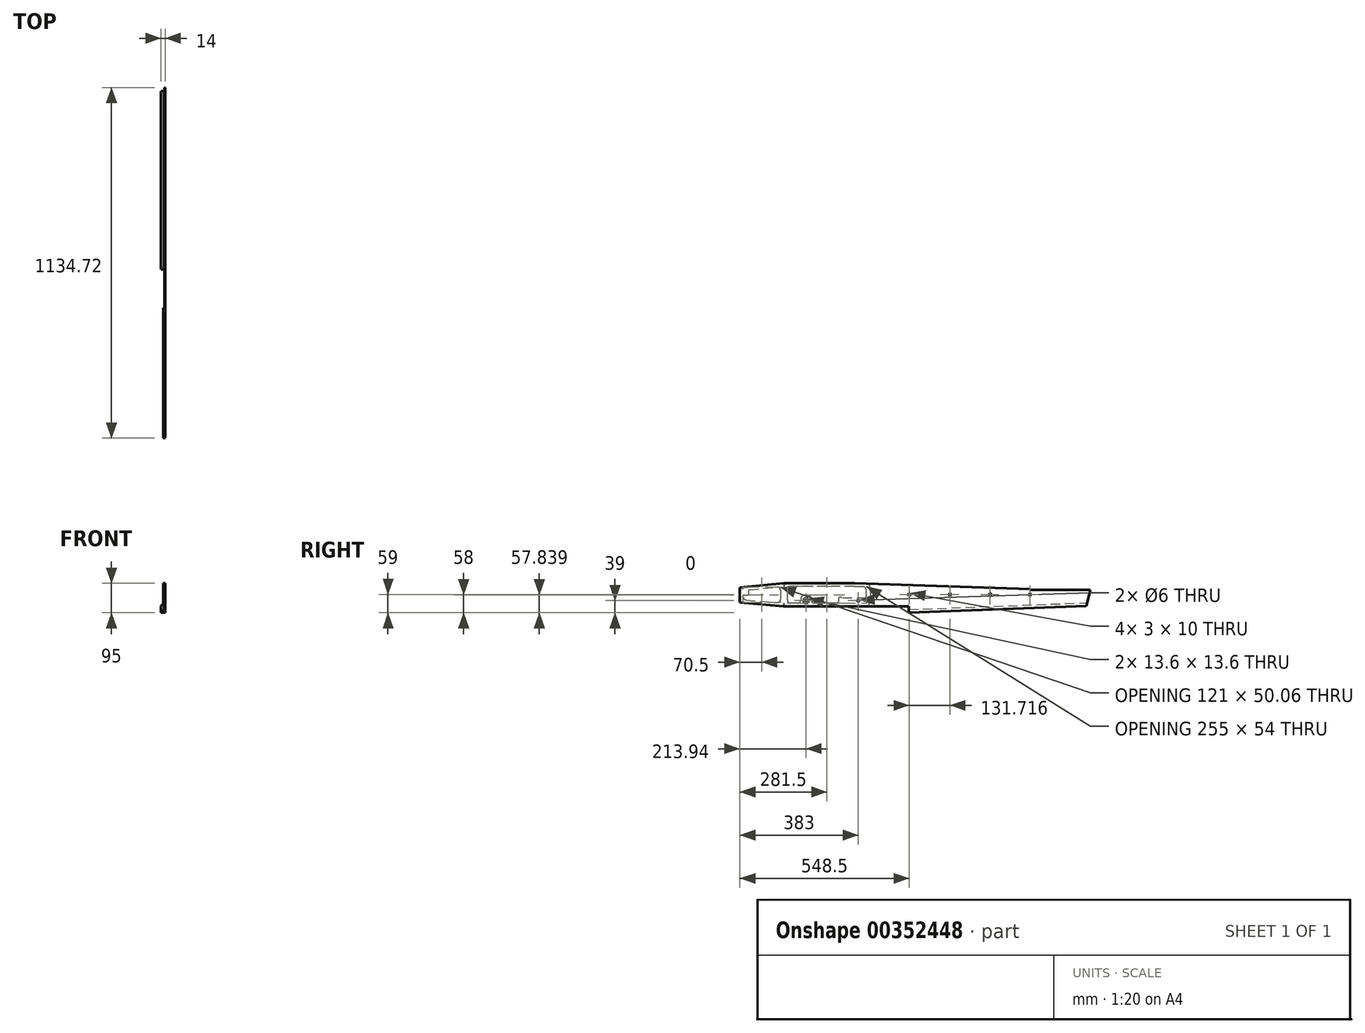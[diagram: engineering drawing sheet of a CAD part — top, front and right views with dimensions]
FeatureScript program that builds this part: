
annotation { "Feature Type Name" : "Feature", "Feature Type Description" : "" }
export const myFeature = defineFeature(function(context is Context, id is Id, definition is map)
    precondition{}
    {
        {
            var Q0;
            Q0=qCreatedBy(makeId("Right.planeOp"),FACE);
            var sketch = newSketch(context, id + "F0", { "sketchPlane" : qUnion([Q0])});
            skLineSegment(sketch, "E0", {"start": v(-571.5, 0) * mm, "end": v(571.5, 0) * mm, "construction": true});
            skLineSegment(sketch, "E1", {"start": v(-571.5, 22) * mm, "end": v(-571.5, -26) * mm});
            skLineSegment(sketch, "E2", {"start": v(-571.5, 22) * mm, "end": v(-430.5, 36) * mm});
            skLineSegment(sketch, "E3", {"start": v(-430.5, 36) * mm, "end": v(-200.5, 36) * mm});
            skLineSegment(sketch, "E4", {"start": v(-200.5, 36) * mm, "end": v(369.22, 18) * mm});
            skLineSegment(sketch, "E5", {"start": v(369.22, 18) * mm, "end": v(369.22, 15) * mm});
            skLineSegment(sketch, "E6", {"start": v(369.22, 15) * mm, "end": v(563.22, 15) * mm});
            skLineSegment(sketch, "E7", {"start": v(-571.5, -26) * mm, "end": v(-430.5, -38) * mm});
            skLineSegment(sketch, "E8", {"start": v(-430.5, -38) * mm, "end": v(-24.5, -38) * mm});
            skLineSegment(sketch, "E9", {"start": v(-24.5, -38) * mm, "end": v(-24.5, -59) * mm});
            skLineSegment(sketch, "E10", {"start": v(-24.5, -59) * mm, "end": v(551.06, -36.59) * mm});
            skLineSegment(sketch, "E11", {"start": v(563.22, 15) * mm, "end": v(551.06, -36.59) * mm});
            skLineSegment(sketch, "E12", {"start": v(-175.5, 35.21) * mm, "end": v(-175.5, -38) * mm, "construction": true});
            skPoint(sketch, "E13", {"position": v(-175.5, -38) * mm});
            skPoint(sketch, "E14", {"position": v(-175.5, 35.21) * mm});
            skLineSegment(sketch, "E15", {"start": v(-458.5, -20) * mm, "end": v(-113.5, -20) * mm, "construction": true});
            skLineSegment(sketch, "E16.bottom", {"start": v(-350.76, -13.2) * mm, "end": v(-364.36, -13.2) * mm});
            skLineSegment(sketch, "E16.top", {"start": v(-350.76, -26.8) * mm, "end": v(-364.36, -26.8) * mm});
            skLineSegment(sketch, "E16.left", {"start": v(-350.76, -13.2) * mm, "end": v(-350.76, -26.8) * mm});
            skLineSegment(sketch, "E16.right", {"start": v(-364.36, -13.2) * mm, "end": v(-364.36, -26.8) * mm});
            skPoint(sketch, "E16.middle", {"position": v(-357.56, -20) * mm});
            skLineSegment(sketch, "E17", {"start": v(369.22, 15) * mm, "end": v(369.22, -43.67) * mm, "construction": true});
            skLineSegment(sketch, "E18", {"start": v(369.22, -5) * mm, "end": v(366.22, -5) * mm});
            skLineSegment(sketch, "E19", {"start": v(366.22, -5) * mm, "end": v(366.22, 5) * mm});
            skLineSegment(sketch, "E20", {"start": v(366.22, 5) * mm, "end": v(369.22, 5) * mm});
            skLineSegment(sketch, "E21.bottom", {"start": v(237.22, 5) * mm, "end": v(240.22, 5) * mm});
            skLineSegment(sketch, "E21.top", {"start": v(237.22, -5) * mm, "end": v(240.22, -5) * mm});
            skLineSegment(sketch, "E21.left", {"start": v(237.22, 5) * mm, "end": v(237.22, -5) * mm});
            skLineSegment(sketch, "E21.right", {"start": v(240.22, 5) * mm, "end": v(240.22, -5) * mm});
            skPoint(sketch, "E21.middle", {"position": v(238.72, 0) * mm});
            skLineSegment(sketch, "E22.bottom", {"start": v(107.22, 5) * mm, "end": v(110.22, 5) * mm});
            skLineSegment(sketch, "E22.top", {"start": v(107.22, -5) * mm, "end": v(110.22, -5) * mm});
            skLineSegment(sketch, "E22.left", {"start": v(107.22, 5) * mm, "end": v(107.22, -5) * mm});
            skLineSegment(sketch, "E22.right", {"start": v(110.22, 5) * mm, "end": v(110.22, -5) * mm});
            skPoint(sketch, "E22.middle", {"position": v(108.72, 0) * mm});
            skLineSegment(sketch, "E23.bottom", {"start": v(-21.5, 5) * mm, "end": v(-24.5, 5) * mm});
            skLineSegment(sketch, "E23.top", {"start": v(-21.5, -5) * mm, "end": v(-24.5, -5) * mm});
            skLineSegment(sketch, "E23.left", {"start": v(-21.5, 5) * mm, "end": v(-21.5, -5) * mm});
            skLineSegment(sketch, "E23.right", {"start": v(-24.5, 5) * mm, "end": v(-24.5, -5) * mm});
            skPoint(sketch, "E23.middle", {"position": v(-23, 0) * mm});
            skLineSegment(sketch, "E24", {"start": v(369.22, 5) * mm, "end": v(369.22, -5) * mm});
            skLineSegment(sketch, "E25", {"start": v(107.22, 26.28) * mm, "end": v(107.22, -53.87) * mm, "construction": true});
            skLineSegment(sketch, "E26", {"start": v(237.22, 22.17) * mm, "end": v(237.22, -48.8) * mm, "construction": true});
            skCircle(sketch, "E27", {"center": v(-188.5, -20) * mm, "radius": 3 * mm});
            skLineSegment(sketch, "E28", {"start": v(-24.5, -38) * mm, "end": v(-24.5, 30.44) * mm, "construction": true});
            skSolve(sketch);
        }
        {
            var Q0;
            Q0=makeQuery(id+"F0.imprint","IMPRINT",FACE,{"disambiguationData":[TD([[makeQuery(id+"F0.imprint","IMPRINT",EDGE,{"derivedFrom":sQuery(id+"F0.wireOp",EDGE,"E1")}),1.0]])]});
            extrude(context, id + "F1", {"entities" : qUnion([Q0]), "offsetDistance" : 25 * mm, "depth" : 3 * mm, "symmetric" : true});
        }
        {
            var Q0;
            Q0=makeQuery(id+"F1.opExtrude","SWEPT_FACE",FACE,{"disambiguationData":[OSD([sQuery(id+"F0.wireOp",EDGE,"E9")])]});
            cPlane(context, id + "F2", {"entities" : qUnion([Q0]), "cplaneType" : CPlaneType.OFFSET, "offset" : 0 * mm, "width" : 150 * mm, "height" : 150 * mm});
        }
        {
            var Q0;
            Q0=qCreatedBy(id+"F2.planeOp",FACE);
            var sketch = newSketch(context, id + "F3", { "sketchPlane" : qUnion([Q0])});
            skLineSegment(sketch, "E29", {"start": v(2.5, -59) * mm, "end": v(12.5, -59) * mm});
            skLineSegment(sketch, "E30", {"start": v(12.5, -59) * mm, "end": v(2.5, -49) * mm});
            skLineSegment(sketch, "E31", {"start": v(2.5, -49) * mm, "end": v(2.5, -59) * mm});
            skLineSegment(sketch, "E32.MirrorCS", {"start": v(-2.5, -49) * mm, "end": v(-2.5, -59) * mm});
            skLineSegment(sketch, "E33.MirrorCS", {"start": v(-2.5, -59) * mm, "end": v(-12.5, -59) * mm});
            skLineSegment(sketch, "E34.MirrorCS", {"start": v(-12.5, -59) * mm, "end": v(-2.5, -49) * mm});
            skSolve(sketch);
        }
        {
            var Q0;
            Q0=makeQuery(id+"F1.opExtrude","SWEPT_FACE",FACE,{"disambiguationData":[OSD([sQuery(id+"F0.wireOp",EDGE,"E11")])]});
            cPlane(context, id + "F4", {"entities" : qUnion([Q0]), "cplaneType" : CPlaneType.OFFSET, "offset" : 0 * mm, "width" : 150 * mm, "height" : 150 * mm});
        }
        {
            var Q0;
            Q0=qCreatedBy(id+"F4.planeOp",FACE);
            var sketch = newSketch(context, id + "F5", { "sketchPlane" : qUnion([Q0])});
            skLineSegment(sketch, "E35", {"start": v(-2.5, 90.74) * mm, "end": v(-12.5, 90.74) * mm});
            skLineSegment(sketch, "E36", {"start": v(-12.5, 90.74) * mm, "end": v(-2.5, 100.74) * mm});
            skLineSegment(sketch, "E37", {"start": v(-2.5, 90.74) * mm, "end": v(-2.5, 100.74) * mm});
            skLineSegment(sketch, "E38.MirrorCS", {"start": v(2.5, 90.74) * mm, "end": v(2.5, 100.74) * mm});
            skLineSegment(sketch, "E39.MirrorCS", {"start": v(2.5, 90.74) * mm, "end": v(12.5, 90.74) * mm});
            skLineSegment(sketch, "E40.MirrorCS", {"start": v(12.5, 90.74) * mm, "end": v(2.5, 100.74) * mm});
            skSolve(sketch);
        }
        {
            var Q0;
            Q0=makeQuery(id+"F3.imprint","IMPRINT",FACE,{"disambiguationData":[TD([[makeQuery(id+"F3.imprint","IMPRINT",EDGE,{"derivedFrom":sQuery(id+"F3.wireOp",EDGE,"E32.MirrorCS")}),-1.0]])]});
            var Q1;
            Q1=makeQuery(id+"F5.imprint","IMPRINT",FACE,{"disambiguationData":[TD([[makeQuery(id+"F5.imprint","IMPRINT",EDGE,{"derivedFrom":sQuery(id+"F5.wireOp",EDGE,"E38.MirrorCS")}),-1.0]])]});
            loft(context, id + "F6", {"sheetProfilesArray" : [{ "sheetProfileEntities" : qUnion([Q0]) }, { "sheetProfileEntities" : qUnion([Q1]) }]});
        }
        {
            var Q0;
            Q0=qCreatedBy(makeId("Right.planeOp"),FACE);
            cPlane(context, id + "F7", {"entities" : qUnion([Q0]), "cplaneType" : CPlaneType.OFFSET, "offset" : 2 * mm, "oppositeDirection" : true, "width" : 150 * mm, "height" : 150 * mm});
        }
        {
            var Q0;
            Q0=qCreatedBy(id+"F7.planeOp",FACE);
            var sketch = newSketch(context, id + "F8", { "sketchPlane" : qUnion([Q0])});
            skLineSegment(sketch, "E41", {"start": v(-571.5, 0) * mm, "end": v(-149.5, 0) * mm, "construction": true});
            skLineSegment(sketch, "E42", {"start": v(-571.5, 12) * mm, "end": v(-571.5, -26) * mm});
            skLineSegment(sketch, "E43", {"start": v(-568.5, 22.3) * mm, "end": v(-430.5, 36) * mm});
            skLineSegment(sketch, "E44", {"start": v(-427.5, 36) * mm, "end": v(-200.5, 36) * mm});
            skLineSegment(sketch, "E45", {"start": v(-200.5, 36) * mm, "end": v(-152.5, 34.35) * mm});
            skLineSegment(sketch, "E46", {"start": v(-571.5, -26) * mm, "end": v(-430.5, -38) * mm});
            skLineSegment(sketch, "E47", {"start": v(-427.5, -38) * mm, "end": v(-152.5, -38) * mm});
            skLineSegment(sketch, "E48.bottom", {"start": v(-364.36, -13.2) * mm, "end": v(-350.76, -13.2) * mm});
            skLineSegment(sketch, "E48.top", {"start": v(-364.36, -26.8) * mm, "end": v(-350.76, -26.8) * mm});
            skLineSegment(sketch, "E48.left", {"start": v(-364.36, -13.2) * mm, "end": v(-364.36, -26.8) * mm});
            skLineSegment(sketch, "E48.right", {"start": v(-350.76, -13.2) * mm, "end": v(-350.76, -26.8) * mm});
            skCircle(sketch, "E49", {"center": v(-188.5, -20) * mm, "radius": 3 * mm});
            skLineSegment(sketch, "E50.top", {"start": v(-149.5, 24.39) * mm, "end": v(-152.5, 24.39) * mm});
            skLineSegment(sketch, "E50.right", {"start": v(-152.5, 34.35) * mm, "end": v(-152.5, 24.39) * mm});
            skLineSegment(sketch, "E51.top", {"start": v(-149.5, -28) * mm, "end": v(-152.5, -28) * mm});
            skLineSegment(sketch, "E51.right", {"start": v(-152.5, -38) * mm, "end": v(-152.5, -28) * mm});
            skLineSegment(sketch, "E52", {"start": v(-149.5, 24.39) * mm, "end": v(-149.5, -28) * mm});
            skLineSegment(sketch, "E53.top", {"start": v(-430.5, 26) * mm, "end": v(-427.5, 26) * mm});
            skLineSegment(sketch, "E53.left", {"start": v(-430.5, 36) * mm, "end": v(-430.5, 26) * mm});
            skLineSegment(sketch, "E53.right", {"start": v(-427.5, 36) * mm, "end": v(-427.5, 26) * mm});
            skLineSegment(sketch, "E54.top", {"start": v(-430.5, -28) * mm, "end": v(-427.5, -28) * mm});
            skLineSegment(sketch, "E54.left", {"start": v(-430.5, -38) * mm, "end": v(-430.5, -28) * mm});
            skLineSegment(sketch, "E54.right", {"start": v(-427.5, -38) * mm, "end": v(-427.5, -28) * mm});
            skLineSegment(sketch, "E55", {"start": v(-571.5, 12) * mm, "end": v(-568.5, 12) * mm});
            skLineSegment(sketch, "E56", {"start": v(-568.5, 12) * mm, "end": v(-568.5, 22.3) * mm});
            skPoint(sketch, "E57.orphan", {"position": v(-571.5, 22) * mm});
            skLineSegment(sketch, "E58", {"start": v(-430.5, 36) * mm, "end": v(-430.5, -38) * mm, "construction": true});
            skLineSegment(sketch, "E59.0", {"start": v(-541.25, 14.95) * mm, "end": v(-451.49, 23.87) * mm});
            skLineSegment(sketch, "E59.2", {"start": v(-552.35, -17.6) * mm, "end": v(-451.35, -26.19) * mm});
            skLineSegment(sketch, "E59.3", {"start": v(-440.5, 13.92) * mm, "end": v(-440.5, -16.23) * mm});
            skPoint(sketch, "E60.visualSharp", {"position": v(-440.5, 24.96) * mm});
            skArc(sketch, "E60.filletArc", {"start": v(-440.5, 13.92) * mm, "mid": v(-443.79, 21.33) * mm, "end": v(-451.49, 23.87) * mm});
            skPoint(sketch, "E61.visualSharp", {"position": v(-440.5, -27.11) * mm});
            skArc(sketch, "E61.filletArc", {"start": v(-451.35, -26.19) * mm, "mid": v(-443.74, -23.6) * mm, "end": v(-440.5, -16.23) * mm});
            skPoint(sketch, "E62.visualSharp", {"position": v(-561.5, -16.81) * mm});
            skArc(sketch, "E62.filletArc", {"start": v(-561.5, -7.63) * mm, "mid": v(-558.86, -14.4) * mm, "end": v(-552.35, -17.6) * mm});
            skPoint(sketch, "E63.visualSharp", {"position": v(-561.5, 12.94) * mm});
            skLineSegment(sketch, "E64", {"start": v(-162.5, -12) * mm, "end": v(-242.5, -12) * mm});
            skLineSegment(sketch, "E65", {"start": v(-242.5, -12) * mm, "end": v(-242.5, -9) * mm});
            skLineSegment(sketch, "E66.top", {"start": v(-350.76, -3.2) * mm, "end": v(-364.36, -3.2) * mm});
            skLineSegment(sketch, "E66.right", {"start": v(-417.5, 16) * mm, "end": v(-417.5, -3.2) * mm});
            skLineSegment(sketch, "E67", {"start": v(-252.5, -14) * mm, "end": v(-252.5, -23.1) * mm});
            skLineSegment(sketch, "E68", {"start": v(-257.4, -28) * mm, "end": v(-330.76, -28) * mm});
            skLineSegment(sketch, "E69", {"start": v(-340.76, -18) * mm, "end": v(-340.76, -13.2) * mm});
            skLineSegment(sketch, "E70", {"start": v(-374.36, -13.2) * mm, "end": v(-374.36, -18) * mm});
            skLineSegment(sketch, "E71", {"start": v(-384.36, -28) * mm, "end": v(-407.5, -28) * mm});
            skLineSegment(sketch, "E72", {"start": v(-417.5, -18) * mm, "end": v(-417.5, -3.2) * mm});
            skLineSegment(sketch, "E73", {"start": v(-200.5, 26) * mm, "end": v(-172.5, 25.04) * mm});
            skPoint(sketch, "E74", {"position": v(-172.5, 25.04) * mm});
            skArc(sketch, "E75", {"start": v(-162.5, 14.7) * mm, "mid": v(-165.4, 21.88) * mm, "end": v(-172.5, 25.04) * mm});
            skPoint(sketch, "E76.start.orphan", {"position": v(-162.5, 24.7) * mm});
            skPoint(sketch, "E77.visualSharp", {"position": v(-252.5, -28) * mm});
            skArc(sketch, "E77.filletArc", {"start": v(-257.4, -28) * mm, "mid": v(-253.94, -26.56) * mm, "end": v(-252.5, -23.1) * mm});
            skPoint(sketch, "E78.visualSharp", {"position": v(-374.36, -28) * mm});
            skArc(sketch, "E78.filletArc", {"start": v(-384.36, -28) * mm, "mid": v(-377.29, -25.07) * mm, "end": v(-374.36, -18) * mm});
            skPoint(sketch, "E79.visualSharp", {"position": v(-340.76, -28) * mm});
            skArc(sketch, "E79.filletArc", {"start": v(-340.76, -18) * mm, "mid": v(-337.83, -25.07) * mm, "end": v(-330.76, -28) * mm});
            skPoint(sketch, "E80.visualSharp", {"position": v(-417.5, -28) * mm});
            skArc(sketch, "E80.filletArc", {"start": v(-417.5, -18) * mm, "mid": v(-414.57, -25.07) * mm, "end": v(-407.5, -28) * mm});
            skPoint(sketch, "E81.visualSharp", {"position": v(-417.5, 26) * mm});
            skArc(sketch, "E81.filletArc", {"start": v(-407.5, 26) * mm, "mid": v(-414.57, 23.07) * mm, "end": v(-417.5, 16) * mm});
            skPoint(sketch, "E82.visualSharp", {"position": v(-340.76, -3.2) * mm});
            skArc(sketch, "E82.filletArc", {"start": v(-340.76, -13.2) * mm, "mid": v(-343.69, -6.13) * mm, "end": v(-350.76, -3.2) * mm});
            skPoint(sketch, "E83.visualSharp", {"position": v(-374.36, -3.2) * mm});
            skArc(sketch, "E83.filletArc", {"start": v(-364.36, -3.2) * mm, "mid": v(-371.43, -6.13) * mm, "end": v(-374.36, -13.2) * mm});
            skLineSegment(sketch, "E84", {"start": v(-242.5, -9) * mm, "end": v(-247.5, -9) * mm});
            skLineSegment(sketch, "E85", {"start": v(-200.5, 26) * mm, "end": v(-407.5, 26) * mm});
            skLineSegment(sketch, "E86", {"start": v(-162.5, -12) * mm, "end": v(-162.5, 14.7) * mm});
            skPoint(sketch, "E87.visualSharp", {"position": v(-252.5, -9) * mm});
            skArc(sketch, "E87.filletArc", {"start": v(-247.5, -9) * mm, "mid": v(-251.04, -10.46) * mm, "end": v(-252.5, -14) * mm});
            skLineSegment(sketch, "E88", {"start": v(-568.5, 12) * mm, "end": v(-553.5, 12) * mm, "construction": true});
            skLineSegment(sketch, "E89", {"start": v(-553.5, 3) * mm, "end": v(-553.5, 12) * mm, "construction": true});
            skLineSegment(sketch, "E90", {"start": v(-553.5, 3) * mm, "end": v(-571.62, 3) * mm, "construction": true});
            skPoint(sketch, "E91.visualSharp", {"position": v(-543.5, 7.49) * mm});
            skPoint(sketch, "E92.visualSharp", {"position": v(-561.5, 7.49) * mm});
            skPoint(sketch, "E93.visualSharp", {"position": v(-543.5, 14.73) * mm});
            skArc(sketch, "E93.filletArc", {"start": v(-541.25, 14.95) * mm, "mid": v(-542.85, 14.15) * mm, "end": v(-543.5, 12.47) * mm});
            skLineSegment(sketch, "E94", {"start": v(-561.5, -7.63) * mm, "end": v(-561.5, -4.5) * mm});
            skLineSegment(sketch, "E95", {"start": v(-559, -2) * mm, "end": v(-546, -2) * mm});
            skLineSegment(sketch, "E96", {"start": v(-543.5, 0.5) * mm, "end": v(-543.5, 12.47) * mm});
            skPoint(sketch, "E97.visualSharp", {"position": v(-543.5, -2) * mm});
            skArc(sketch, "E97.filletArc", {"start": v(-546, -2) * mm, "mid": v(-544.23, -1.27) * mm, "end": v(-543.5, 0.5) * mm});
            skPoint(sketch, "E98.visualSharp", {"position": v(-561.5, -2) * mm});
            skArc(sketch, "E98.filletArc", {"start": v(-559, -2) * mm, "mid": v(-560.77, -2.73) * mm, "end": v(-561.5, -4.5) * mm});
            skSolve(sketch);
        }
        {
            var Q0;
            Q0 = qSketchRegion(id + "F8", true);
            var Q1;
            Q1=makeQuery(id+"F1.opExtrude","CAP_FACE",FACE,{"disambiguationData":[OSD([sQuery(id+"F0.wireOp",EDGE,"E1"),sQuery(id+"F0.wireOp",EDGE,"E2"),sQuery(id+"F0.wireOp",EDGE,"E3"),sQuery(id+"F0.wireOp",EDGE,"E4"),sQuery(id+"F0.wireOp",EDGE,"E5"),sQuery(id+"F0.wireOp",EDGE,"E6"),sQuery(id+"F0.wireOp",EDGE,"E7"),sQuery(id+"F0.wireOp",EDGE,"E8"),sQuery(id+"F0.wireOp",EDGE,"E9"),sQuery(id+"F0.wireOp",EDGE,"E10"),sQuery(id+"F0.wireOp",EDGE,"E11"),sQuery(id+"F0.wireOp",EDGE,"E16.bottom"),sQuery(id+"F0.wireOp",EDGE,"E16.top"),sQuery(id+"F0.wireOp",EDGE,"E16.left"),sQuery(id+"F0.wireOp",EDGE,"E16.right"),sQuery(id+"F0.wireOp",EDGE,"E18"),sQuery(id+"F0.wireOp",EDGE,"E19"),sQuery(id+"F0.wireOp",EDGE,"E20"),sQuery(id+"F0.wireOp",EDGE,"E21.bottom"),sQuery(id+"F0.wireOp",EDGE,"E21.top"),sQuery(id+"F0.wireOp",EDGE,"E21.left"),sQuery(id+"F0.wireOp",EDGE,"E21.right"),sQuery(id+"F0.wireOp",EDGE,"E22.bottom"),sQuery(id+"F0.wireOp",EDGE,"E22.top"),sQuery(id+"F0.wireOp",EDGE,"E22.left"),sQuery(id+"F0.wireOp",EDGE,"E22.right"),sQuery(id+"F0.wireOp",EDGE,"E23.bottom"),sQuery(id+"F0.wireOp",EDGE,"E23.top"),sQuery(id+"F0.wireOp",EDGE,"E23.left"),sQuery(id+"F0.wireOp",EDGE,"E23.right"),sQuery(id+"F0.wireOp",EDGE,"zscQRFKG-8hHy-9WlW-DJEY-TXOdkuwEjGPw.bottom"),sQuery(id+"F0.wireOp",EDGE,"zscQRFKG-8hHy-9WlW-DJEY-TXOdkuwEjGPw.top"),sQuery(id+"F0.wireOp",EDGE,"zscQRFKG-8hHy-9WlW-DJEY-TXOdkuwEjGPw.left"),sQuery(id+"F0.wireOp",EDGE,"zscQRFKG-8hHy-9WlW-DJEY-TXOdkuwEjGPw.right"),sQuery(id+"F0.wireOp",EDGE,"E24"),sQuery(id+"F0.wireOp",EDGE,"E27")])],"isStart":false});
            extrude(context, id + "F9", {"entities" : qUnion([Q0, Q1]), "operationType" : NewBodyOperationType.ADD, "oppositeDirection" : true, "depth" : 3 * mm});
        }
    });
